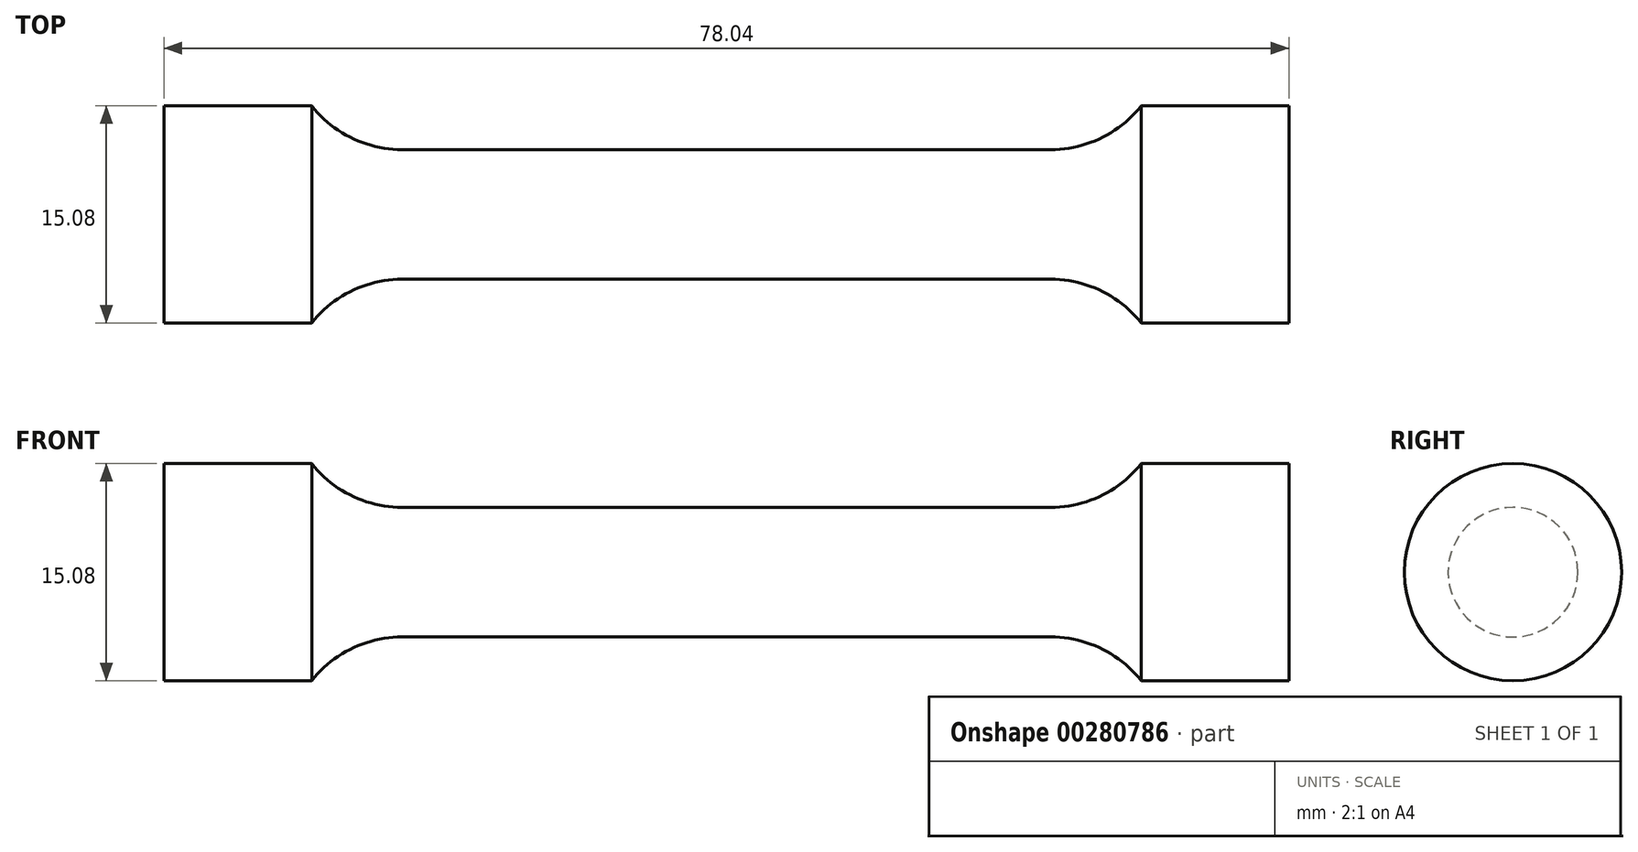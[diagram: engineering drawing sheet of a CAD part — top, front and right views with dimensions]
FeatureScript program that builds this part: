
annotation { "Feature Type Name" : "Feature", "Feature Type Description" : "" }
export const myFeature = defineFeature(function(context is Context, id is Id, definition is map)
    precondition{}
    {
        {
            var Q0;
            Q0=qCreatedBy(makeId("Front.planeOp"),FACE);
            var sketch = newSketch(context, id + "F0", { "sketchPlane" : qUnion([Q0])});
            skLineSegment(sketch, "E0", {"start": v(0, 4.5) * mm, "end": v(22.5, 4.5) * mm});
            skArc(sketch, "E1", {"start": v(22.5, 4.5) * mm, "mid": v(25.98, 5.3) * mm, "end": v(28.77, 7.54) * mm});
            skLineSegment(sketch, "E2", {"start": v(28.77, 7.54) * mm, "end": v(39.02, 7.54) * mm});
            skLineSegment(sketch, "E3", {"start": v(39.02, 7.54) * mm, "end": v(39.02, 0) * mm});
            skLineSegment(sketch, "E4.MirrorCS", {"start": v(0, 4.5) * mm, "end": v(-22.5, 4.5) * mm});
            skLineSegment(sketch, "E5.MirrorCS", {"start": v(-39.02, 7.54) * mm, "end": v(-39.02, 0) * mm});
            skLineSegment(sketch, "E6.MirrorCS", {"start": v(-28.77, 7.54) * mm, "end": v(-39.02, 7.54) * mm});
            skArc(sketch, "E7.MirrorCS", {"start": v(-22.5, 4.5) * mm, "mid": v(-25.98, 5.3) * mm, "end": v(-28.77, 7.54) * mm});
            skLineSegment(sketch, "E8", {"start": v(-39.02, 0) * mm, "end": v(39.02, 0) * mm});
            skSolve(sketch);
        }
        {
            var Q0;
            Q0 = qSketchRegion(id + "F0", true);
            var Q1;
            Q1=sQuery(id+"F0.wireOp",EDGE,"E8");
            revolve(context, id + "F1", {"entities" : qUnion([Q0]), "axis" : qUnion([Q1]), "revolveType" : RevolveType.FULL});
        }
    });
